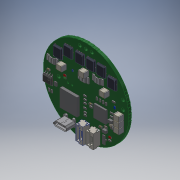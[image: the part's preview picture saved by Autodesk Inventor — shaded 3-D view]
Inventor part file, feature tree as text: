
AUTODESK INVENTOR PART (.ipt)
format: ipt  version: 2019.4 (Build 234330000, 330)  size: 6,927,872 bytes
history: native  units: mm
features: other x220, extrude x91, sketch x1, shell x1
ambient origin geometry x8: Origin, YZ Plane, XZ Plane, XY Plane, X Axis, Y Axis, Z Axis, Center Point
bodies: Solid1 (feature_tree), Solid2 (feature_tree), Solid3 (feature_tree), Solid4 (feature_tree), Solid5 (feature_tree), Solid6 (feature_tree), Solid7 (feature_tree), Solid8 (feature_tree), Solid9 (feature_tree), Solid10 (feature_tree), Solid11 (feature_tree), Solid12 (feature_tree), Solid13 (feature_tree), Solid14 (feature_tree), Solid15 (feature_tree), Solid16 (feature_tree), Solid17 (feature_tree), Solid18 (feature_tree), Solid19 (feature_tree), Solid20 (feature_tree), Solid21 (feature_tree), Solid22 (feature_tree), Solid23 (feature_tree), Solid24 (feature_tree), Solid25 (feature_tree), Solid26 (feature_tree), Solid27 (feature_tree), Solid28 (feature_tree), Solid29 (feature_tree), Solid30 (feature_tree), Solid31 (feature_tree), Solid32 (feature_tree), Solid33 (feature_tree), Solid34 (feature_tree), Solid35 (feature_tree), Solid36 (feature_tree), Solid37 (feature_tree), Solid38 (feature_tree), Solid39 (feature_tree), Solid40 (feature_tree), Solid41 (feature_tree), Solid42 (feature_tree), Solid43 (feature_tree), Solid44 (feature_tree), Solid45 (feature_tree), Solid46 (feature_tree), Solid47 (feature_tree), Solid48 (feature_tree), Solid49 (feature_tree), Solid50 (feature_tree), Solid51 (feature_tree), Solid52 (feature_tree), Solid53 (feature_tree), Solid54 (feature_tree), Solid55 (feature_tree), Solid56 (feature_tree), Solid57 (feature_tree), Solid58 (feature_tree), Solid59 (feature_tree), Solid60 (feature_tree), Solid61 (feature_tree), Solid62 (feature_tree), Solid63 (feature_tree), Solid64 (feature_tree), Solid65 (feature_tree), Solid66 (feature_tree), Solid67 (feature_tree), Solid68 (feature_tree), Solid69 (feature_tree), Solid70 (feature_tree), Solid71 (feature_tree), Solid72 (feature_tree), Solid73 (feature_tree), Solid74 (feature_tree), Solid75 (feature_tree), Solid76 (feature_tree), Solid77 (feature_tree), Solid78 (feature_tree), Solid79 (feature_tree), Solid80 (feature_tree), Solid81 (feature_tree), Solid82 (feature_tree), Solid83 (feature_tree), Solid84 (feature_tree), Solid85 (feature_tree), Solid86 (feature_tree), Solid87 (feature_tree), Solid88 (feature_tree), Solid89 (feature_tree), Solid90 (feature_tree), Solid91 (feature_tree), Solid92 (feature_tree), Solid93 (feature_tree), Solid94 (feature_tree), Solid95 (feature_tree), Solid96 (feature_tree), Solid97 (feature_tree), Solid98 (feature_tree), Solid99 (feature_tree), Solid100 (feature_tree), Solid101 (feature_tree), Solid102 (feature_tree), Solid103 (feature_tree), Solid104 (feature_tree), Solid105 (feature_tree), Solid106 (feature_tree), Solid107 (feature_tree), Solid108 (feature_tree), Solid109 (feature_tree), Solid110 (feature_tree), Solid111 (feature_tree), Solid112 (feature_tree), Solid113 (feature_tree), Solid114 (feature_tree), Solid115 (feature_tree), Solid116 (feature_tree), Solid117 (feature_tree), Solid118 (feature_tree), Solid119 (feature_tree), Solid120 (feature_tree), Solid121 (feature_tree), Solid122 (feature_tree), Solid123 (feature_tree), Solid124 (feature_tree), Solid125 (feature_tree), Solid126 (feature_tree), Solid127 (feature_tree), Solid128 (feature_tree), Solid129 (feature_tree), Solid130 (feature_tree), Solid131 (feature_tree), Solid132 (feature_tree), Solid133 (feature_tree), Solid134 (feature_tree), Solid135 (feature_tree), Solid136 (feature_tree), Solid137 (feature_tree), Solid138 (feature_tree), Solid139 (feature_tree), Solid140 (feature_tree), Solid141 (feature_tree), Solid142 (feature_tree), Solid143 (feature_tree), Solid144 (feature_tree), Solid145 (feature_tree), Solid146 (feature_tree), Solid147 (feature_tree), Solid148 (feature_tree), Solid149 (feature_tree), Solid150 (feature_tree), Solid151 (feature_tree), Solid152 (feature_tree), Solid153 (feature_tree), Solid154 (feature_tree), Solid155 (feature_tree), Solid156 (feature_tree), Solid157 (feature_tree), Solid158 (feature_tree), Solid159 (feature_tree), Solid160 (feature_tree), Solid161 (feature_tree), Solid162 (feature_tree), Solid163 (feature_tree), Solid164 (feature_tree), Solid165 (feature_tree), Solid166 (feature_tree), Solid167 (feature_tree), Solid168 (feature_tree), Solid169 (feature_tree), Solid170 (feature_tree), Solid171 (feature_tree), Solid172 (feature_tree), Solid173 (feature_tree), Solid174 (feature_tree), Solid175 (feature_tree), Solid176 (feature_tree), Solid177 (feature_tree), Solid178 (feature_tree), Solid179 (feature_tree), Solid180 (feature_tree), Solid181 (feature_tree), Solid182 (feature_tree), Solid183 (feature_tree), Solid184 (feature_tree), Solid185 (feature_tree), Solid186 (feature_tree), Solid187 (feature_tree), Solid188 (feature_tree), Solid189 (feature_tree), Solid190 (feature_tree), Solid191 (feature_tree), Solid192 (feature_tree), Solid193 (feature_tree), Solid194 (feature_tree), Solid195 (feature_tree), Solid196 (feature_tree), Solid197 (feature_tree), Solid198 (feature_tree), Solid199 (feature_tree), Solid200 (feature_tree), Solid201 (feature_tree), Solid202 (feature_tree), Solid203 (feature_tree), Solid204 (feature_tree), Solid205 (feature_tree), Solid206 (feature_tree), Solid207 (feature_tree), Solid208 (feature_tree), Solid209 (feature_tree), Solid210 (feature_tree), Solid211 (feature_tree), Solid212 (feature_tree), Solid213 (feature_tree), Solid214 (feature_tree), Solid215 (feature_tree), Solid216 (feature_tree), Solid217 (feature_tree), Solid218 (feature_tree), Solid219 (feature_tree), Solid220 (feature_tree), Solid221 (feature_tree), Solid222 (feature_tree), Solid223 (feature_tree), Solid224 (feature_tree), Solid225 (feature_tree), Solid226 (feature_tree), Solid227 (feature_tree), Solid228 (feature_tree), Solid229 (feature_tree), Solid230 (feature_tree), Solid231 (feature_tree), Solid232 (feature_tree), Solid233 (feature_tree), Solid234 (feature_tree), Solid235 (feature_tree), Solid236 (feature_tree), Solid237 (feature_tree), Solid238 (feature_tree), Solid239 (feature_tree), Solid240 (feature_tree), Solid241 (feature_tree), Solid242 (feature_tree), Solid243 (feature_tree), Solid244 (feature_tree), Solid245 (feature_tree), Solid246 (feature_tree), Solid247 (feature_tree), Solid248 (feature_tree), Solid249 (feature_tree), Solid250 (feature_tree), Solid251 (feature_tree), Solid252 (feature_tree), Solid253 (feature_tree), Solid254 (feature_tree), Solid255 (feature_tree), Solid256 (feature_tree), Solid257 (feature_tree), Solid258 (feature_tree), Solid259 (feature_tree), Solid260 (feature_tree), Solid261 (feature_tree), Solid262 (feature_tree), Solid263 (feature_tree), Solid264 (feature_tree), Solid265 (feature_tree), Solid266 (feature_tree), Solid267 (feature_tree), Solid268 (feature_tree), Solid269 (feature_tree), Solid270 (feature_tree), Solid271 (feature_tree), Solid272 (feature_tree), Solid273 (feature_tree), Solid274 (feature_tree), Solid275 (feature_tree), Solid276 (feature_tree), Solid277 (feature_tree), Solid278 (feature_tree), Solid279 (feature_tree), Solid280 (feature_tree), Solid281 (feature_tree), Solid282 (feature_tree), Solid283 (feature_tree), Solid284 (feature_tree), Solid285 (feature_tree), Solid286 (feature_tree), Solid287 (feature_tree), Solid288 (feature_tree), Solid289 (feature_tree), Solid290 (feature_tree), Solid291 (feature_tree), Solid292 (feature_tree), Solid293 (feature_tree), Solid294 (feature_tree), Solid295 (feature_tree), Solid296 (feature_tree), Solid297 (feature_tree), Solid298 (feature_tree), Solid299 (feature_tree), Solid300 (feature_tree), Solid301 (feature_tree), Solid302 (feature_tree), Solid303 (feature_tree), Solid304 (feature_tree), Solid305 (feature_tree), Solid306 (feature_tree), Solid307 (feature_tree), Solid308 (feature_tree), Solid309 (feature_tree)
feature tree (313):
  extrude  "Extrusion1"  Depth=30.0mm TaperAngle=0.0deg
  sketch  "Sketch1"  dims[d0=50.0mm d1=30.0mm d2=30.0mm d3=0.0mm d4=0.0mm d5=16.000001mm]
  other  "Board_1:1"
  extrude  "Extruded_2:1"  Depth=16.000001mm
  extrude  "Extruded_2:2"  [1 undecoded]
  other  "JST_BM04B-GHS-TBT_7:1"
  other  "0603_resistor_9:1"
  other  "0603_resistor_9:2"
  other  "TER2-2_11:1"
  other  "TER2-1_12:1"
  other  "TER2_13:1"
  other  "TER2-3_14:1"
  other  "TER2-4_15:1"
  other  "HOUSING-1_17:1"
  shell  "SHELL_18:1"  [1 undecoded]
  extrude  "Extruded_21:1"  [1 undecoded]
  extrude  "Extruded_24:1"  [1 undecoded]
  extrude  "Extruded_27:1"  [1 undecoded]
  extrude  "Extruded_29:1"  [1 undecoded]
  extrude  "Extruded_29:2"  [1 undecoded]
  other  "0603_cap_33:1"
  extrude  "Extruded_35:1"  [1 undecoded]
  extrude  "Extruded_37:1"  [1 undecoded]
  extrude  "Extruded_35:2"  [1 undecoded]
  other  "User_Library-DFN5x6_SO8FL_Extruded_41:1"
  other  "User_Library-DFN5x6_SO8FL_Extruded_2_43:1"
  other  "User_Library-DFN5x6_SO8FL_Extruded_2_43:2"
  other  "User_Library-DFN5x6_SO8FL_Extruded_41:2"
  other  "User_Library-DFN5x6_SO8FL_Cylinder_47:1"
  other  "User_Library-DFN5x6_SO8FL_Extruded_3_49:1"
  other  "User_Library-DFN5x6_SO8FL_Extruded_4_51:1"
  other  "User_Library-DFN5x6_SO8FL_Extruded_5_53:1"
  other  "User_Library-DFN5x6_SO8FL_Extruded_5_53:2"
  other  "User_Library-DFN5x6_SO8FL_Extruded_5_53:3"
  other  "User_Library-DFN5x6_SO8FL_Extruded_5_53:4"
  other  "User_Library-DFN5x6_SO8FL_Extruded_6_58:1"
  extrude  "Extruded_63:1"  [1 undecoded]
  other  "0603_resistor_66:1"
  other  "0603_resistor_66:2"
  other  "0603_resistor_68:1"
  other  "0603_resistor_68:2"
  other  "0603_resistor_70:1"
  other  "0603_resistor_70:2"
  other  "0603_resistor_72:1"
  other  "0603_resistor_72:2"
  extrude  "Extruded_74:1"  [1 undecoded]
  extrude  "Extruded_76:1"  [1 undecoded]
  extrude  "Extruded_76:2"  [1 undecoded]
  extrude  "Extruded_80:1"  [1 undecoded]
  extrude  "Extruded_82:1"  [1 undecoded]
  extrude  "Extruded_82:2"  [1 undecoded]
  extrude  "Extruded_82:3"  [1 undecoded]
  extrude  "Extruded_82:4"  [1 undecoded]
  extrude  "Extruded_80:2"  [1 undecoded]
  other  "0603_cap_90:1"
  other  "0603_cap_92:1"
  other  "0603_cap_94:1"
  extrude  "Extruded_82:5"  [1 undecoded]
  extrude  "Extruded_82:6"  [1 undecoded]
  extrude  "Extruded_80:3"  [1 undecoded]
  extrude  "Extruded_100:1"  [1 undecoded]
  extrude  "Extruded_100:2"  [1 undecoded]
  extrude  "Extruded_103:1"  [1 undecoded]
  extrude  "Extruded_100:3"  [1 undecoded]
  extrude  "Extruded_100:4"  [1 undecoded]
  extrude  "Extruded_103:2"  [1 undecoded]
  extrude  "Extruded_100:5"  [1 undecoded]
  extrude  "Extruded_100:6"  [1 undecoded]
  extrude  "Extruded_103:3"  [1 undecoded]
  extrude  "Extruded_80:4"  [1 undecoded]
  extrude  "Extruded_82:7"  [1 undecoded]
  extrude  "Extruded_82:8"  [1 undecoded]
  extrude  "Extruded_80:5"  [1 undecoded]
  extrude  "Extruded_82:9"  [1 undecoded]
  extrude  "Extruded_82:10"  [1 undecoded]
  extrude  "Extruded_80:6"  [1 undecoded]
  extrude  "Extruded_82:11"  [1 undecoded]
  extrude  "Extruded_82:12"  [1 undecoded]
  extrude  "Extruded_80:7"  [1 undecoded]
  extrude  "Extruded_82:13"  [1 undecoded]
  extrude  "Extruded_82:14"  [1 undecoded]
  extrude  "Extruded_80:8"  [1 undecoded]
  extrude  "Extruded_82:15"  [1 undecoded]
  extrude  "Extruded_82:16"  [1 undecoded]
  extrude  "Extruded_80:9"  [1 undecoded]
  extrude  "Extruded_82:17"  [1 undecoded]
  extrude  "Extruded_82:18"  [1 undecoded]
  extrude  "Extruded_138:1"  [1 undecoded]
  extrude  "Extruded_140:1"  [1 undecoded]
  extrude  "Extruded_140:2"  [1 undecoded]
  other  "User_Library-MR30PW-M_144:1"
  extrude  "Extruded_146:1"  [1 undecoded]
  extrude  "Extruded_149:1"  [1 undecoded]
  extrude  "Extruded_152:1"  [1 undecoded]
  other  "User_Library-SOT-223-2_PIN_SOT-223_2_1_155:1"
  other  "User_Library-SOT-223-2_SOT-223_1_156:1"
  other  "User_Library-SOT-223-2_PIN_SOT-223_2_1_157:1"
  other  "User_Library-SOT-223-2_PIN_SOT-223_1_158:1"
  other  "User_Library-SOT-223-2_PIN_SOT-223_2_1_159:1"
  other  "0603_resistor_162:1"
  other  "0603_resistor_162:2"
  other  "0603_resistor_164:1"
  other  "0603_resistor_164:2"
  other  "0603_resistor_166:1"
  other  "0603_resistor_166:2"
  other  "0603_resistor_168:1"
  other  "0603_resistor_168:2"
  other  "0603_resistor_170:1"
  other  "0603_resistor_170:2"
  other  "0603_resistor_172:1"
  other  "0603_resistor_172:2"
  other  "0603_resistor_174:1"
  other  "0603_resistor_174:2"
  other  "0603_resistor_176:1"
  other  "0603_resistor_176:2"
  other  "0603_resistor_178:1"
  other  "0603_resistor_178:2"
  other  "0603_resistor_180:1"
  other  "0603_resistor_180:2"
  extrude  "Extruded_35:3"  [1 undecoded]
  extrude  "Extruded_37:2"  [1 undecoded]
  extrude  "Extruded_35:4"  [1 undecoded]
  other  "0603_resistor_186:1"
  other  "0603_resistor_186:2"
  other  "CSS2H-2512K-2L00F_188:1"
  other  "0603_resistor_190:1"
  other  "0603_resistor_190:2"
  other  "0603_resistor_192:1"
  other  "0603_resistor_192:2"
  other  "0603_resistor_194:1"
  other  "0603_resistor_194:2"
  other  "0603_resistor_196:1"
  other  "0603_resistor_196:2"
  other  "CSS2H-2512K-2L00F_198:1"
  other  "0603_resistor_200:1"
  other  "0603_resistor_200:2"
  other  "0603_resistor_202:1"
  other  "0603_resistor_202:2"
  other  "0603_resistor_204:1"
  other  "0603_resistor_204:2"
  other  "0603_resistor_206:1"
  other  "0603_resistor_206:2"
  other  "0603_resistor_208:1"
  other  "0603_resistor_208:2"
  other  "CSS2H-2512K-2L00F_210:1"
  other  "0402_resistor_212:1"
  other  "0402_resistor_212:2"
  other  "0603_resistor_214:1"
  other  "0603_resistor_214:2"
  other  "0603_resistor_216:1"
  other  "0603_resistor_216:2"
  other  "0603_resistor_218:1"
  other  "0603_resistor_218:2"
  other  "0603_resistor_220:1"
  other  "0603_resistor_220:2"
  other  "0603_resistor_222:1"
  other  "0603_resistor_222:2"
  other  "0603_resistor_224:1"
  other  "0603_resistor_224:2"
  other  "0603_resistor_226:1"
  other  "0603_resistor_226:2"
  other  "0603_resistor_228:1"
  other  "0603_resistor_228:2"
  other  "0603_resistor_230:1"
  other  "0603_resistor_230:2"
  other  "0603_resistor_232:1"
  other  "0603_resistor_232:2"
  other  "User_Library-DFN5x6_SO8FL_Extruded_41:3"
  other  "User_Library-DFN5x6_SO8FL_Extruded_2_43:3"
  other  "User_Library-DFN5x6_SO8FL_Extruded_2_43:4"
  other  "User_Library-DFN5x6_SO8FL_Extruded_41:4"
  other  "User_Library-DFN5x6_SO8FL_Cylinder_47:2"
  other  "User_Library-DFN5x6_SO8FL_Extruded_3_49:2"
  other  "User_Library-DFN5x6_SO8FL_Extruded_4_51:2"
  other  "User_Library-DFN5x6_SO8FL_Extruded_5_53:5"
  other  "User_Library-DFN5x6_SO8FL_Extruded_5_53:6"
  other  "User_Library-DFN5x6_SO8FL_Extruded_5_53:7"
  other  "User_Library-DFN5x6_SO8FL_Extruded_5_53:8"
  other  "User_Library-DFN5x6_SO8FL_Extruded_6_58:2"
  other  "User_Library-DFN5x6_SO8FL_Extruded_41:5"
  other  "User_Library-DFN5x6_SO8FL_Extruded_2_43:5"
  other  "User_Library-DFN5x6_SO8FL_Extruded_2_43:6"
  other  "User_Library-DFN5x6_SO8FL_Extruded_41:6"
  other  "User_Library-DFN5x6_SO8FL_Cylinder_47:3"
  other  "User_Library-DFN5x6_SO8FL_Extruded_3_49:3"
  other  "User_Library-DFN5x6_SO8FL_Extruded_4_51:3"
  other  "User_Library-DFN5x6_SO8FL_Extruded_5_53:9"
  other  "User_Library-DFN5x6_SO8FL_Extruded_5_53:10"
  other  "User_Library-DFN5x6_SO8FL_Extruded_5_53:11"
  other  "User_Library-DFN5x6_SO8FL_Extruded_5_53:12"
  other  "User_Library-DFN5x6_SO8FL_Extruded_6_58:3"
  other  "body_30xx_238:1"
  other  "land_pattern_30xx_239:1"
  other  "land_pattern_30xx_240:1"
  other  "FER_0603_243:1"
  other  "JST_BM05B-GHS-TBT_245:1"
  other  "LED_0603_Base_RED_247:1"
  other  "LED_0603_Base_RED_247:2"
  other  "LED_0603_Lens_RED_248:1"
  extrude  "Extruded_250:1"  [1 undecoded]
  other  "LED_0603_Lens_BLUE_255:1"
  other  "LED_0603_Base_BLUE_256:1"
  other  "LED_0603_Base_BLUE_256:2"
  other  "LED_0603_Lens_GREEN_258:1"
  other  "LED_0603_Base_GREEN_259:1"
  other  "LED_0603_Base_GREEN_259:2"
  other  "LED_0603_Base_RED_261:1"
  other  "LED_0603_Base_RED_261:2"
  other  "LED_0603_Lens_RED_262:1"
  other  "0402_cap_264:1"
  other  "0603_cap_266:1"
  other  "0603_cap_268:1"
  other  "0402_cap_270:1"
  other  "0603_cap_272:1"
  extrude  "Extruded_82:19"  [1 undecoded]
  extrude  "Extruded_82:20"  [1 undecoded]
  extrude  "Extruded_80:10"  [1 undecoded]
  extrude  "Extruded_29:3"  [1 undecoded]
  extrude  "Extruded_29:4"  [1 undecoded]
  extrude  "Extruded_27:2"  [1 undecoded]
  extrude  "Extruded_82:21"  [1 undecoded]
  extrude  "Extruded_82:22"  [1 undecoded]
  extrude  "Extruded_80:11"  [1 undecoded]
  other  "0603_cap_286:1"
  extrude  "Extruded_63:2"  [1 undecoded]
  other  "0603_cap_290:1"
  other  "0603_cap_292:1"
  extrude  "Extruded_294:1"  [1 undecoded]
  extrude  "Extruded_294:2"  [1 undecoded]
  extrude  "Extruded_297:1"  [1 undecoded]
  other  "0603_cap_300:1"
  extrude  "Extruded_294:3"  [1 undecoded]
  extrude  "Extruded_294:4"  [1 undecoded]
  extrude  "Extruded_297:2"  [1 undecoded]
  other  "0603_cap_306:1"
  extrude  "Extruded_29:5"  [1 undecoded]
  extrude  "Extruded_29:6"  [1 undecoded]
  extrude  "Extruded_27:3"  [1 undecoded]
  other  "0603_cap_312:1"
  other  "0603_cap_314:1"
  other  "0603_cap_316:1"
  other  "0603_cap_318:1"
  other  "0603_cap_320:1"
  other  "0603_cap_322:1"
  other  "0603_cap_324:1"
  other  "0603_cap_326:1"
  other  "0603_cap_328:1"
  other  "0603_cap_330:1"
  other  "User_Library-XT30-_curved_332:1"
  other  "User_Library-XT30-_curved_332:2"
  other  "User_Library-XT30-_curved_332:3"
  extrude  "Extruded_80:12"  [1 undecoded]
  extrude  "Extruded_82:23"  [1 undecoded]
  extrude  "Extruded_82:24"  [1 undecoded]
  extrude  "Extruded_100:7"  [1 undecoded]
  extrude  "Extruded_100:8"  [1 undecoded]
  extrude  "Extruded_103:4"  [1 undecoded]
  extrude  "Extruded_342:1"  [1 undecoded]
  other  "BODY_M08A_35_345:1"
  other  "LEAD_M08A_57_346:1"
  other  "LEAD_M08A_57_347:1"
  other  "LEAD_M08A_57_348:1"
  other  "LEAD_M08A_57_349:1"
  other  "LEAD_M08A_57_350:1"
  other  "LEAD_M08A_57_351:1"
  other  "LEAD_M08A_57_352:1"
  other  "LEAD_M08A_57_353:1"
  other  "MANIFOLD_SOLID_BREP_2784_354:1"
  other  "MANIFOLD_SOLID_BREP_2935_355:1"
  other  "MANIFOLD_SOLID_BREP_3086_356:1"
  other  "MANIFOLD_SOLID_BREP_3237_357:1"
  extrude  "Extruded_362:1"  [1 undecoded]
  extrude  "Extruded_365:1"  [1 undecoded]
  extrude  "Extruded_368:1"  [1 undecoded]
  extrude  "Extruded_370:1"  [1 undecoded]
  other  "User_Library-DFN5x6_SO8FL_Extruded_41:7"
  other  "User_Library-DFN5x6_SO8FL_Extruded_2_43:7"
  other  "User_Library-DFN5x6_SO8FL_Extruded_2_43:8"
  other  "User_Library-DFN5x6_SO8FL_Extruded_41:8"
  other  "User_Library-DFN5x6_SO8FL_Cylinder_47:4"
  other  "User_Library-DFN5x6_SO8FL_Extruded_3_49:4"
  other  "User_Library-DFN5x6_SO8FL_Extruded_4_51:4"
  other  "User_Library-DFN5x6_SO8FL_Extruded_5_53:13"
  other  "User_Library-DFN5x6_SO8FL_Extruded_5_53:14"
  other  "User_Library-DFN5x6_SO8FL_Extruded_5_53:15"
  other  "User_Library-DFN5x6_SO8FL_Extruded_5_53:16"
  other  "User_Library-DFN5x6_SO8FL_Extruded_6_58:4"
  other  "User_Library-DFN5x6_SO8FL_Extruded_41:9"
  other  "User_Library-DFN5x6_SO8FL_Extruded_2_43:9"
  other  "User_Library-DFN5x6_SO8FL_Extruded_2_43:10"
  other  "User_Library-DFN5x6_SO8FL_Extruded_41:10"
  other  "User_Library-DFN5x6_SO8FL_Cylinder_47:5"
  other  "User_Library-DFN5x6_SO8FL_Extruded_3_49:5"
  other  "User_Library-DFN5x6_SO8FL_Extruded_4_51:5"
  other  "User_Library-DFN5x6_SO8FL_Extruded_5_53:17"
  other  "User_Library-DFN5x6_SO8FL_Extruded_5_53:18"
  other  "User_Library-DFN5x6_SO8FL_Extruded_5_53:19"
  other  "User_Library-DFN5x6_SO8FL_Extruded_5_53:20"
  other  "User_Library-DFN5x6_SO8FL_Extruded_6_58:5"
  other  "User_Library-DFN5x6_SO8FL_Extruded_41:11"
  other  "User_Library-DFN5x6_SO8FL_Extruded_2_43:11"
  other  "User_Library-DFN5x6_SO8FL_Extruded_2_43:12"
  other  "User_Library-DFN5x6_SO8FL_Extruded_41:12"
  other  "User_Library-DFN5x6_SO8FL_Cylinder_47:6"
  other  "User_Library-DFN5x6_SO8FL_Extruded_3_49:6"
  other  "User_Library-DFN5x6_SO8FL_Extruded_4_51:6"
  other  "User_Library-DFN5x6_SO8FL_Extruded_5_53:21"
  other  "User_Library-DFN5x6_SO8FL_Extruded_5_53:22"
  other  "User_Library-DFN5x6_SO8FL_Extruded_5_53:23"
  other  "User_Library-DFN5x6_SO8FL_Extruded_5_53:24"
  other  "User_Library-DFN5x6_SO8FL_Extruded_6_58:6"
  other  "Composite1"
  other  "Srf1"
note: 90 required parameter values undecoded (feature->parameter linkage not recoverable at this tier; creation-order binding heuristic only, values carry confidence <= 0.55)
